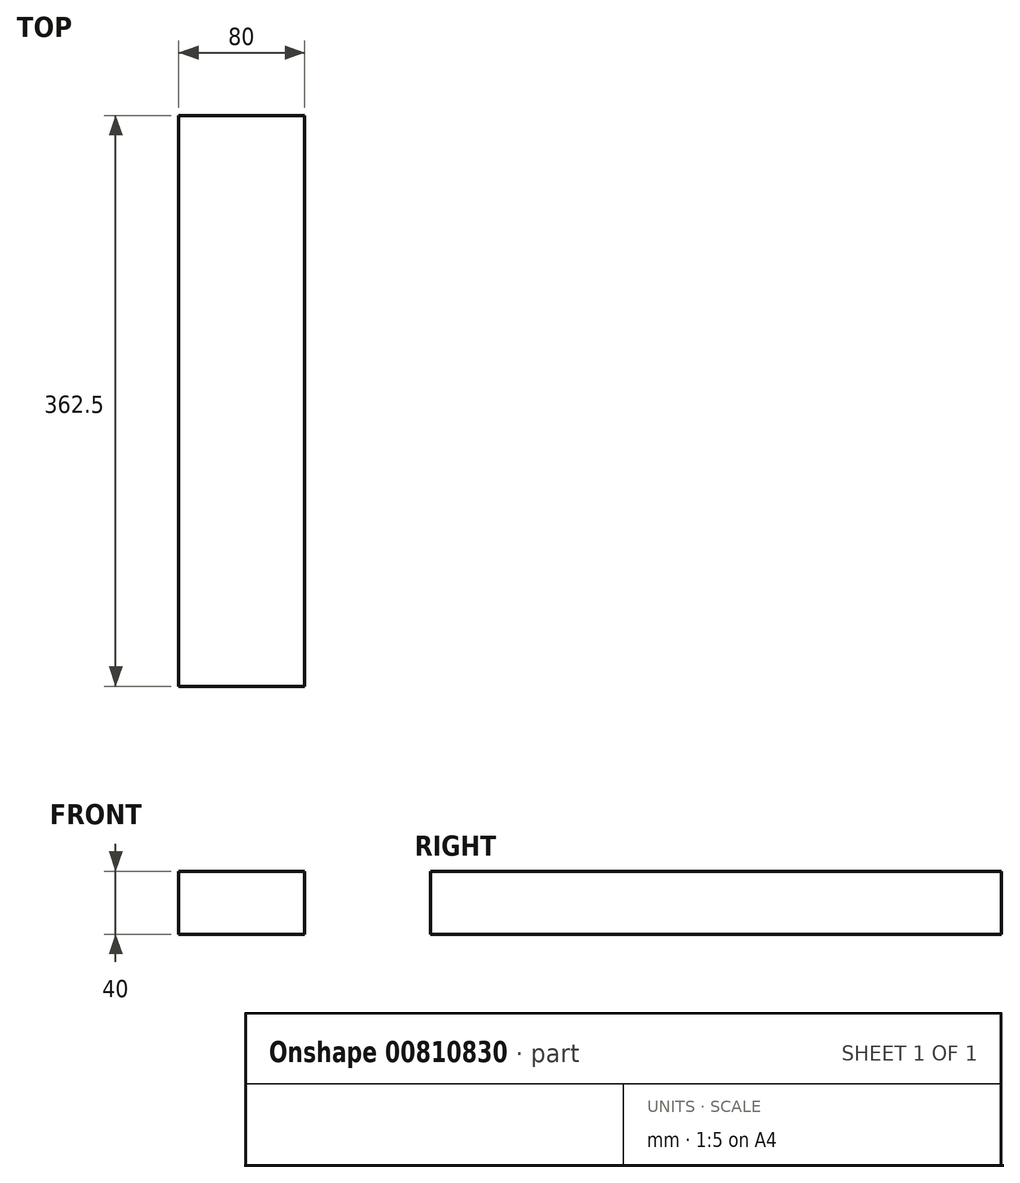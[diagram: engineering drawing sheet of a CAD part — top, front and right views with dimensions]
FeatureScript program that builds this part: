
annotation { "Feature Type Name" : "Feature", "Feature Type Description" : "" }
export const myFeature = defineFeature(function(context is Context, id is Id, definition is map)
    precondition{}
    {
        {
            var Q0;
            Q0=qCreatedBy(makeId("Front.planeOp"),FACE);
            var sketch = newSketch(context, id + "F0", { "sketchPlane" : qUnion([Q0])});
            skLineSegment(sketch, "E0.bottom", {"start": v(40, 20) * mm, "end": v(-40, 20) * mm});
            skLineSegment(sketch, "E0.top", {"start": v(40, -20) * mm, "end": v(-40, -20) * mm});
            skLineSegment(sketch, "E0.left", {"start": v(40, 20) * mm, "end": v(40, -20) * mm});
            skLineSegment(sketch, "E0.right", {"start": v(-40, 20) * mm, "end": v(-40, -20) * mm});
            skPoint(sketch, "E0.middle", {"position": v(0, 0) * mm});
            skSolve(sketch);
        }
        {
            var Q0;
            Q0=makeQuery(id+"F0.imprint","IMPRINT",FACE,{"disambiguationData":[TD([[makeQuery(id+"F0.imprint","IMPRINT",EDGE,{"derivedFrom":sQuery(id+"F0.wireOp",EDGE,"E0.bottom")}),1.0]])]});
            extrude(context, id + "F1", {"entities" : qUnion([Q0]), "endBound" : BoundingType.SYMMETRIC, "depth" : 362.5 * mm, "offsetDistance" : 25 * mm});
        }
    });
